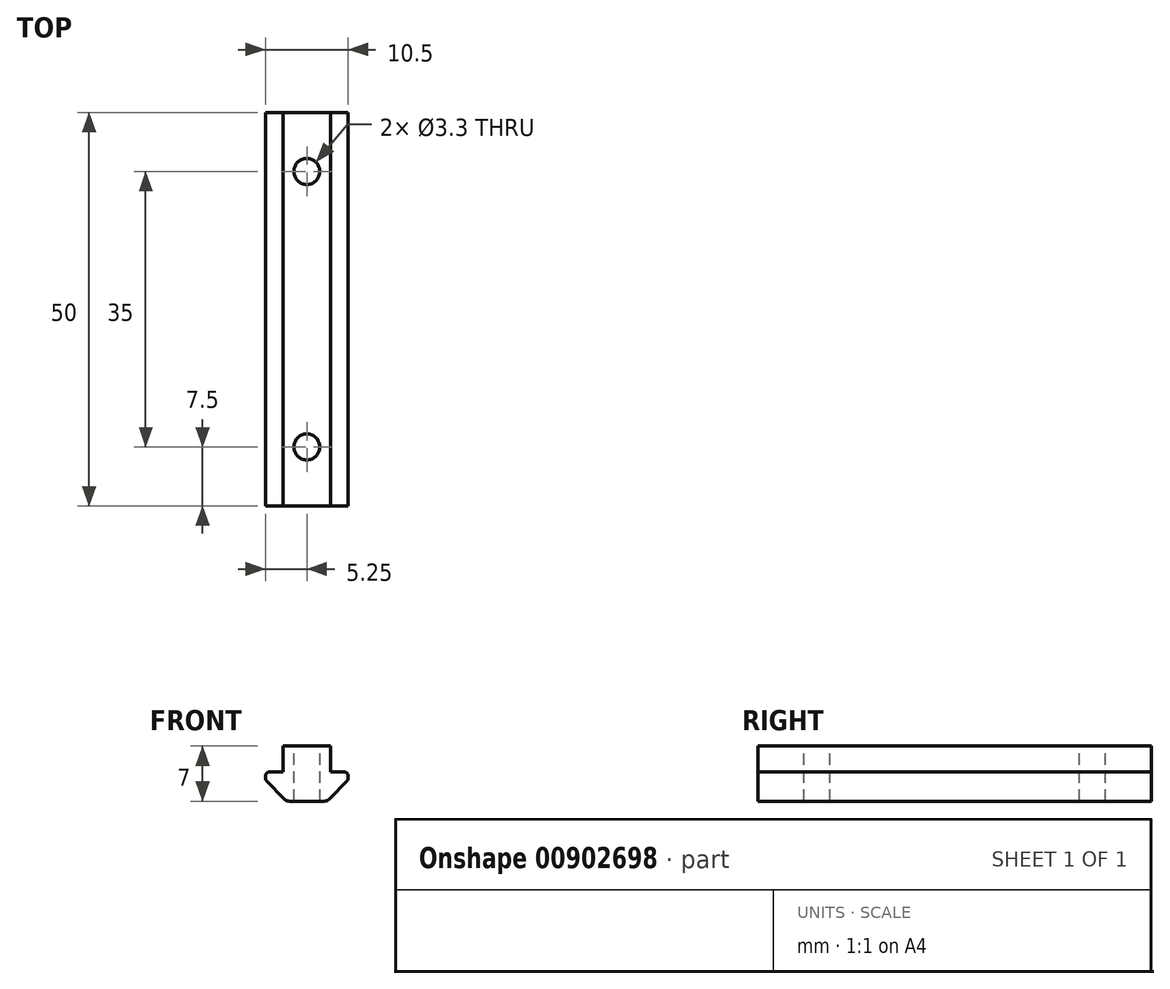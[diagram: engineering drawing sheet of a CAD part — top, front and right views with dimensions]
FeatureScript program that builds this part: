
annotation { "Feature Type Name" : "Feature", "Feature Type Description" : "" }
export const myFeature = defineFeature(function(context is Context, id is Id, definition is map)
    precondition{}
    {
        {
            var Q0;
            Q0=qCreatedBy(makeId("Front.planeOp"),FACE);
            var sketch = newSketch(context, id + "F0", { "sketchPlane" : qUnion([Q0])});
            skLineSegment(sketch, "E0", {"start": v(-2.2, 0) * mm, "end": v(2.2, 0) * mm});
            skLineSegment(sketch, "E1", {"start": v(2.92, 0.3) * mm, "end": v(5.1, 2.55) * mm});
            skLineSegment(sketch, "E2", {"start": v(5.25, 2.9) * mm, "end": v(5.25, 3.2) * mm});
            skLineSegment(sketch, "E3", {"start": v(4.75, 3.7) * mm, "end": v(3, 3.7) * mm});
            skLineSegment(sketch, "E4", {"start": v(3, 3.7) * mm, "end": v(3, 7) * mm});
            skLineSegment(sketch, "E5", {"start": v(3, 7) * mm, "end": v(-3, 7) * mm});
            skLineSegment(sketch, "E6", {"start": v(-2.92, 0.3) * mm, "end": v(-5.1, 2.55) * mm});
            skLineSegment(sketch, "E7", {"start": v(-5.25, 2.9) * mm, "end": v(-5.25, 3.2) * mm});
            skLineSegment(sketch, "E8", {"start": v(-4.75, 3.7) * mm, "end": v(-3, 3.7) * mm});
            skLineSegment(sketch, "E9", {"start": v(-3, 3.7) * mm, "end": v(-3, 7) * mm});
            skPoint(sketch, "E10.visualSharp", {"position": v(-2.62, 0) * mm});
            skArc(sketch, "E10.filletArc", {"start": v(-2.92, 0.3) * mm, "mid": v(-2.6, 0.08) * mm, "end": v(-2.2, 0) * mm});
            skPoint(sketch, "E11.visualSharp", {"position": v(2.63, 0) * mm});
            skArc(sketch, "E11.filletArc", {"start": v(2.2, 0) * mm, "mid": v(2.6, 0.08) * mm, "end": v(2.92, 0.3) * mm});
            skPoint(sketch, "E12.visualSharp", {"position": v(-5.25, 2.7) * mm});
            skArc(sketch, "E12.filletArc", {"start": v(-5.25, 2.9) * mm, "mid": v(-5.21, 2.71) * mm, "end": v(-5.1, 2.55) * mm});
            skPoint(sketch, "E13.visualSharp", {"position": v(-5.25, 3.7) * mm});
            skArc(sketch, "E13.filletArc", {"start": v(-4.75, 3.7) * mm, "mid": v(-5.1, 3.55) * mm, "end": v(-5.25, 3.2) * mm});
            skPoint(sketch, "E14.visualSharp", {"position": v(5.25, 2.7) * mm});
            skArc(sketch, "E14.filletArc", {"start": v(5.1, 2.55) * mm, "mid": v(5.21, 2.71) * mm, "end": v(5.25, 2.9) * mm});
            skPoint(sketch, "E15.visualSharp", {"position": v(5.25, 3.7) * mm});
            skArc(sketch, "E15.filletArc", {"start": v(5.25, 3.2) * mm, "mid": v(5.1, 3.55) * mm, "end": v(4.75, 3.7) * mm});
            skLineSegment(sketch, "E16", {"start": v(0, 0) * mm, "end": v(0, 7) * mm, "construction": true});
            skSolve(sketch);
        }
        {
            var Q0;
            Q0=qSketchRegion(id+"F0",true);
            extrude(context, id + "F1", {"entities" : qUnion([Q0]), "depth" : 50 * mm, "offsetDistance" : 25 * mm});
        }
        {
            var Q0;
            Q0=makeQuery(id+"F1.opExtrude","SWEPT_FACE",FACE,{"disambiguationData":[OSD([sQuery(id+"F0.wireOp",EDGE,"E5")])]});
            var sketch = newSketch(context, id + "F2", { "sketchPlane" : qUnion([Q0])});
            skLineSegment(sketch, "E17", {"start": v(0, 0) * mm, "end": v(0, -7.5) * mm, "construction": true});
            skLineSegment(sketch, "E18", {"start": v(0, -7.5) * mm, "end": v(0, -42.5) * mm, "construction": true});
            skLineSegment(sketch, "E19", {"start": v(0, -42.5) * mm, "end": v(0, -50) * mm, "construction": true});
            skPoint(sketch, "E20", {"position": v(0, -7.5) * mm});
            skPoint(sketch, "E21", {"position": v(0, -42.5) * mm});
            skSolve(sketch);
        }
        {
            var Q0;
            Q0=sQuery(id+"F2.wireOp",VERTEX,"E21");
            var Q1;
            Q1=sQuery(id+"F2.wireOp",VERTEX,"E20");
            var Q2;
            Q2=makeQuery(id+"F1.opExtrude","SWEPT_BODY",BODY,{"disambiguationData":[OSD([sQuery(id+"F0.wireOp",EDGE,"E0"),sQuery(id+"F0.wireOp",EDGE,"E1"),sQuery(id+"F0.wireOp",EDGE,"E2"),sQuery(id+"F0.wireOp",EDGE,"E3"),sQuery(id+"F0.wireOp",EDGE,"E4"),sQuery(id+"F0.wireOp",EDGE,"E5"),sQuery(id+"F0.wireOp",EDGE,"E6"),sQuery(id+"F0.wireOp",EDGE,"E7"),sQuery(id+"F0.wireOp",EDGE,"E8"),sQuery(id+"F0.wireOp",EDGE,"E9"),sQuery(id+"F0.wireOp",EDGE,"E10.filletArc"),sQuery(id+"F0.wireOp",EDGE,"E11.filletArc"),sQuery(id+"F0.wireOp",EDGE,"E12.filletArc"),sQuery(id+"F0.wireOp",EDGE,"E13.filletArc"),sQuery(id+"F0.wireOp",EDGE,"E14.filletArc"),sQuery(id+"F0.wireOp",EDGE,"E15.filletArc")])]});
            hole(context, id + "F3", {"style" : HoleStyle.SIMPLE, "endStyle" : HoleEndStyle.THROUGH, "standardTappedOrClearance" : lookupTablePath({ "standard" : "ISO", "engagement" : "75%", "pitch" : "0.7 mm", "size" : "M4", "type" : "Tapped" }), "standardBlindInLast" : lookupTablePath({ "standard" : "ISO", "engagement" : "75%", "pitch" : "0.7 mm", "size" : "M4", "type" : "Tapped" }), "holeDiameter" : 3.3 * mm, "majorDiameter" : 4 * mm, "showTappedDepth" : true, "isTappedThrough" : true, "tappedDepth" : 20 * mm, "tapClearance" : 3, "locations" : qUnion([Q0, Q1]), "scope" : qUnion([Q2])});
        }
    });
